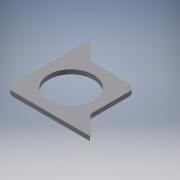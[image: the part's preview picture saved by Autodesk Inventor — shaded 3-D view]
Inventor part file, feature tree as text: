
AUTODESK INVENTOR PART (.ipt)
format: ipt  version: 2016 (Build 200138000, 138)  size: 135,168 bytes
history: native  units: mm
features: extrude x3, sketch x3, fillet x1
ambient origin geometry x8: Origin, YZ Plane, XZ Plane, XY Plane, X Axis, Y Axis, Z Axis, Center Point
bodies: Solid1 (feature_tree)
feature tree (7):
  extrude  "Extrusion1"  Depth=90.0mm
  extrude  "Extrusion2"  Depth=6.0mm TaperAngle=0.0deg
  extrude  "Extrusion3"  Depth=6.0mm TaperAngle=0.0deg
  fillet  "Fillet1"  Radius=6.0mm
  sketch  "Sketch1"  dims[d0=90.0mm d1=90.0mm]
  sketch  "Sketch2"  dims[d2=10.0mm d3=6.0mm d4=0.0mm]
  sketch  "Sketch3"  dims[d5=61.0mm d6=6.0mm d7=0.0mm d9=6.0mm d10=0.0mm d13=53.5mm d15=7.0mm]
